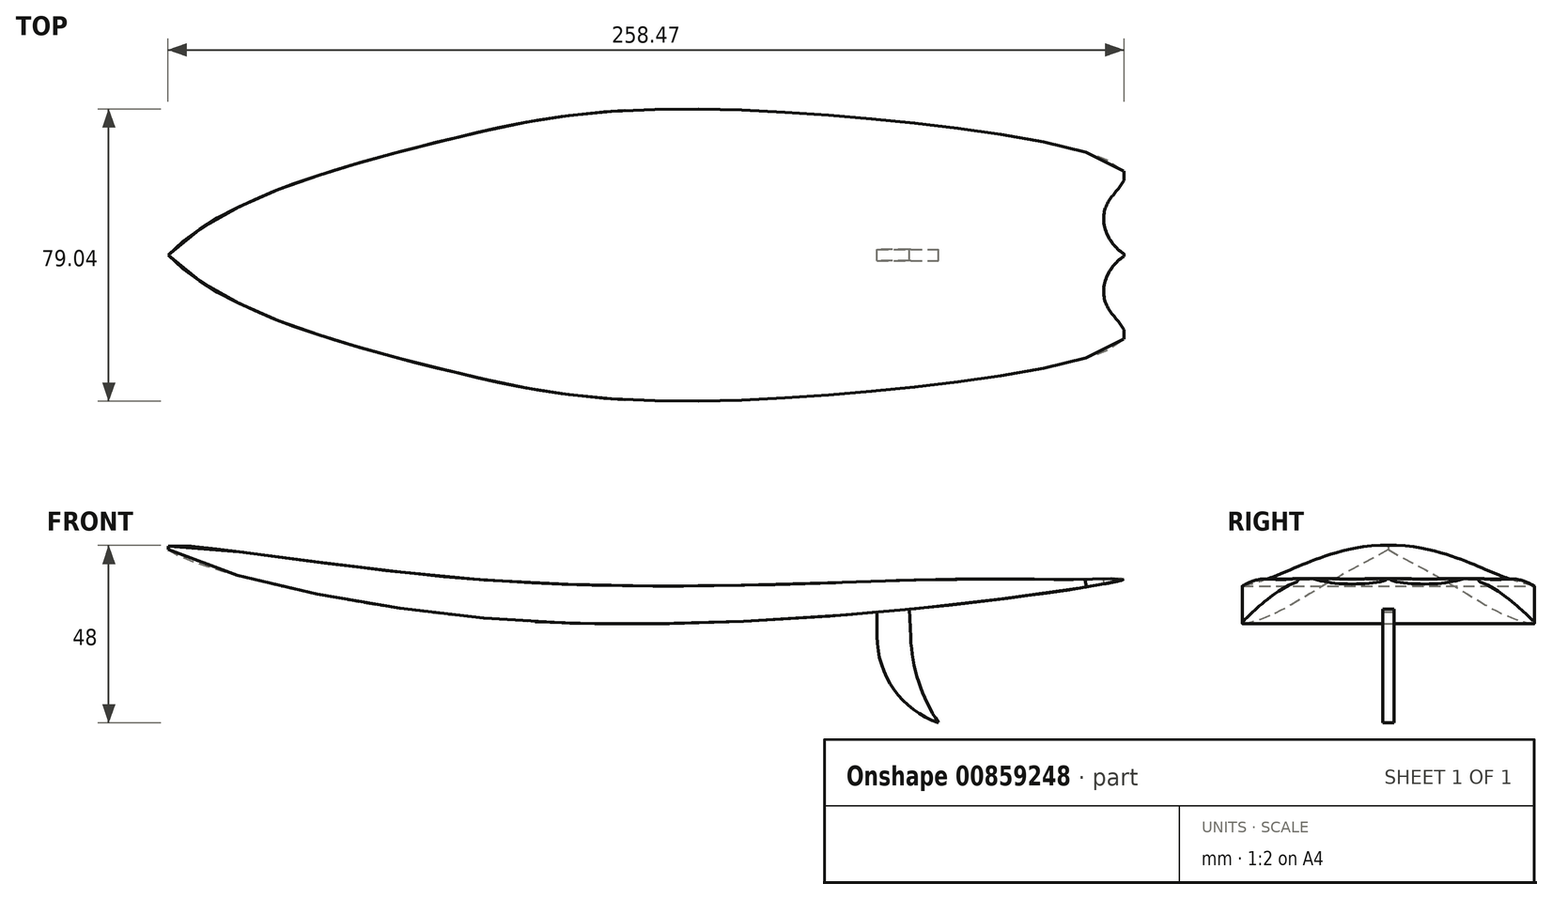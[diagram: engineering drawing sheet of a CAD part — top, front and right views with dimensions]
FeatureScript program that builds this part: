
annotation { "Feature Type Name" : "Feature", "Feature Type Description" : "" }
export const myFeature = defineFeature(function(context is Context, id is Id, definition is map)
    precondition{}
    {
        {
            var Q0;
            Q0=qCreatedBy(makeId("Front.planeOp"),FACE);
            var sketch = newSketch(context, id + "F0", { "sketchPlane" : qUnion([Q0])});
            skFitSpline(sketch, "E0", {"points": [v(-105.56, 8.76) * mm, v(-22.17, 0) * mm, v(105.84, 0) * mm, v(144.44, 0) * mm, v(153.14, 0) * mm, v(-9.76, -11.24) * mm, v(-105.56, 8.76) * mm]});
            skSolve(sketch);
        }
        {
            var Q0;
            Q0=qSketchRegion(id+"F0",true);
            extrude(context, id + "F1", {"entities" : qUnion([Q0]), "endBound" : BoundingType.SYMMETRIC, "depth" : 100 * mm});
        }
        {
            var Q0;
            Q0=qCreatedBy(makeId("Top.planeOp"),FACE);
            var sketch = newSketch(context, id + "F2", { "sketchPlane" : qUnion([Q0])});
            skFitSpline(sketch, "E1", {"points": [v(-105.3, 0) * mm, v(-32.34, 30.58) * mm, v(43.95, 39.4) * mm, v(153.3, 22.36) * mm, v(148.3, 13.06) * mm, v(153.66, 0) * mm], "startDerivative": vector(170.58, 180.81) * mm, "endDerivative": vector(133.82, -80.12) * mm});
            skLineSegment(sketch, "E2", {"start": v(153.66, 0) * mm, "end": v(-105.3, 0) * mm, "construction": true});
            skFitSpline(sketch, "E3.MirrorCS", {"points": [v(-105.3, 0) * mm, v(-32.34, -30.58) * mm, v(43.95, -39.4) * mm, v(153.3, -22.36) * mm, v(148.3, -13.06) * mm, v(153.66, 0) * mm], "startDerivative": vector(170.58, -180.81) * mm, "endDerivative": vector(133.82, 80.12) * mm});
            skSolve(sketch);
        }
        {
            var Q0;
            Q0=qSketchRegion(id+"F2",true);
            extrude(context, id + "F3", {"entities" : qUnion([Q0]), "operationType" : NewBodyOperationType.INTERSECT, "endBound" : BoundingType.SYMMETRIC, "depth" : 800 * mm});
        }
        {
            var Q0;
            Q0=qCreatedBy(makeId("Front.planeOp"),FACE);
            var sketch = newSketch(context, id + "F4", { "sketchPlane" : qUnion([Q0])});
            skLineSegment(sketch, "E4", {"start": v(86.42, -7.47) * mm, "end": v(86.42, -15.43) * mm});
            skArc(sketch, "E5", {"start": v(86.42, -15.43) * mm, "mid": v(91, -29.8) * mm, "end": v(103.08, -38.84) * mm});
            skArc(sketch, "E6", {"start": v(95.5, -15.73) * mm, "mid": v(97.7, -27.8) * mm, "end": v(103.08, -38.84) * mm});
            skLineSegment(sketch, "E7", {"start": v(95.5, -15.73) * mm, "end": v(95.1, -6.92) * mm});
            skLineSegment(sketch, "E8", {"start": v(95.1, -6.92) * mm, "end": v(86.42, -7.47) * mm});
            skSolve(sketch);
        }
        {
            var Q0;
            Q0=makeQuery(id+"F4.imprint","IMPRINT",FACE,{"disambiguationData":[TD([[makeQuery(id+"F4.imprint","IMPRINT",EDGE,{"derivedFrom":sQuery(id+"F4.wireOp",EDGE,"E4")}),1.0]])]});
            extrude(context, id + "F5", {"entities" : qUnion([Q0]), "operationType" : NewBodyOperationType.ADD, "endBound" : BoundingType.SYMMETRIC, "depth" : 3 * mm});
        }
    });
